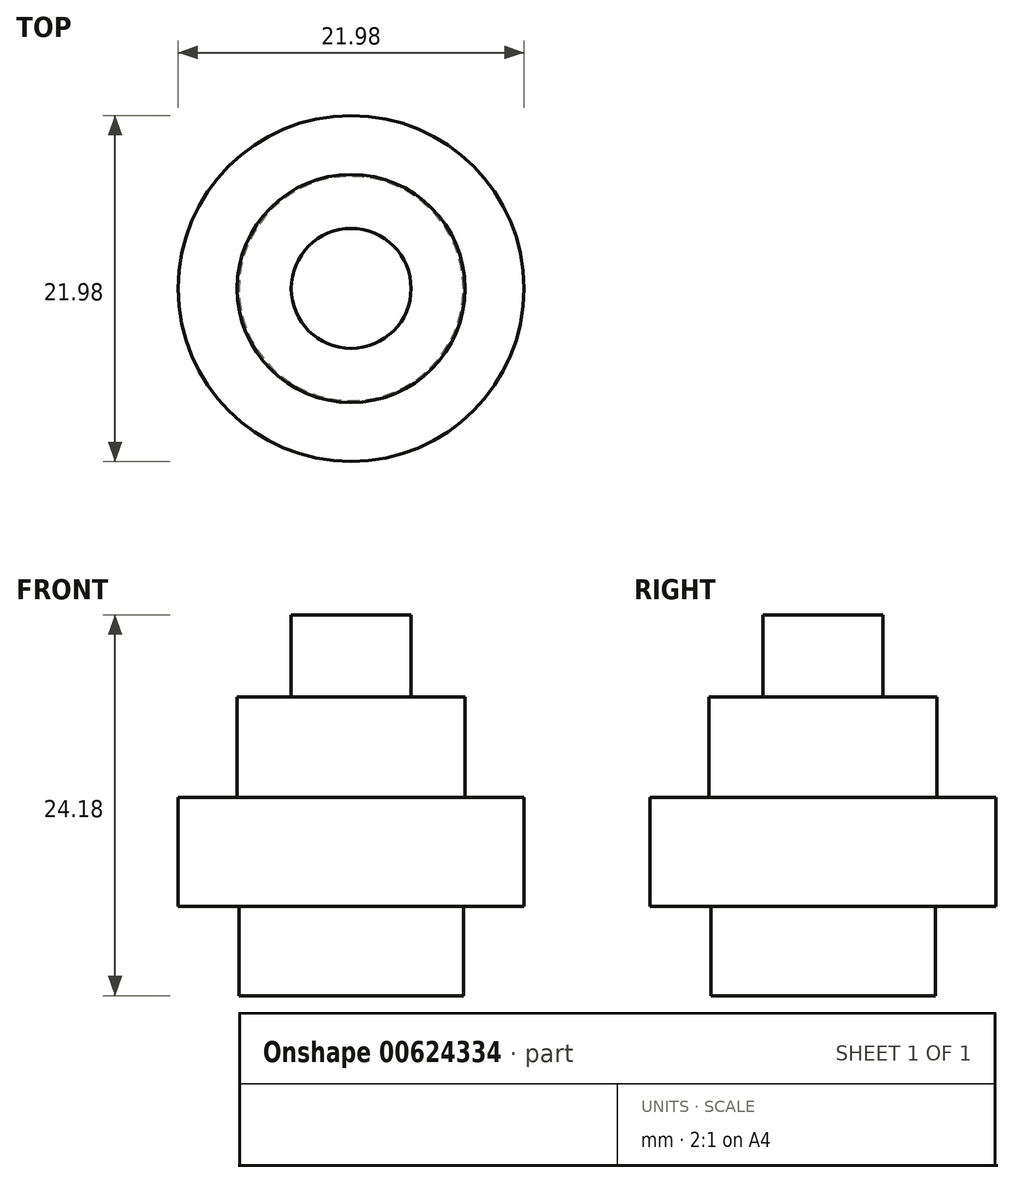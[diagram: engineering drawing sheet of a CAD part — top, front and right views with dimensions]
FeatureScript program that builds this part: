
annotation { "Feature Type Name" : "Feature", "Feature Type Description" : "" }
export const myFeature = defineFeature(function(context is Context, id is Id, definition is map)
    precondition{}
    {
        {
            var Q0;
            Q0=qCreatedBy(makeId("Front.planeOp"),FACE);
            var sketch = newSketch(context, id + "F0", { "sketchPlane" : qUnion([Q0])});
            skLineSegment(sketch, "E0", {"start": v(0, 0) * mm, "end": v(0, 24.18) * mm});
            skLineSegment(sketch, "E1", {"start": v(0, 24.18) * mm, "end": v(3.8, 24.18) * mm});
            skLineSegment(sketch, "E2", {"start": v(3.8, 24.18) * mm, "end": v(3.8, 18.97) * mm});
            skLineSegment(sketch, "E3", {"start": v(3.8, 18.97) * mm, "end": v(7.24, 18.97) * mm});
            skLineSegment(sketch, "E4", {"start": v(7.24, 18.97) * mm, "end": v(7.24, 12.6) * mm});
            skLineSegment(sketch, "E5", {"start": v(7.24, 12.6) * mm, "end": v(10.99, 12.6) * mm});
            skLineSegment(sketch, "E6", {"start": v(10.99, 12.6) * mm, "end": v(10.99, 5.66) * mm});
            skLineSegment(sketch, "E7", {"start": v(10.99, 5.66) * mm, "end": v(7.12, 5.66) * mm});
            skLineSegment(sketch, "E8", {"start": v(7.12, 5.66) * mm, "end": v(7.12, 0) * mm});
            skLineSegment(sketch, "E9", {"start": v(7.12, 0) * mm, "end": v(0, 0) * mm});
            skSolve(sketch);
        }
        {
            var Q0;
            Q0=makeQuery(id+"F0.imprint","IMPRINT",FACE,{"disambiguationData":[TD([[makeQuery(id+"F0.imprint","IMPRINT",EDGE,{"derivedFrom":sQuery(id+"F0.wireOp",EDGE,"E0")}),-1.0]])]});
            var Q1;
            Q1=sQuery(id+"F0.wireOp",EDGE,"E0");
            revolve(context, id + "F1", {"entities" : qUnion([Q0]), "axis" : qUnion([Q1]), "revolveType" : RevolveType.FULL});
        }
    });
